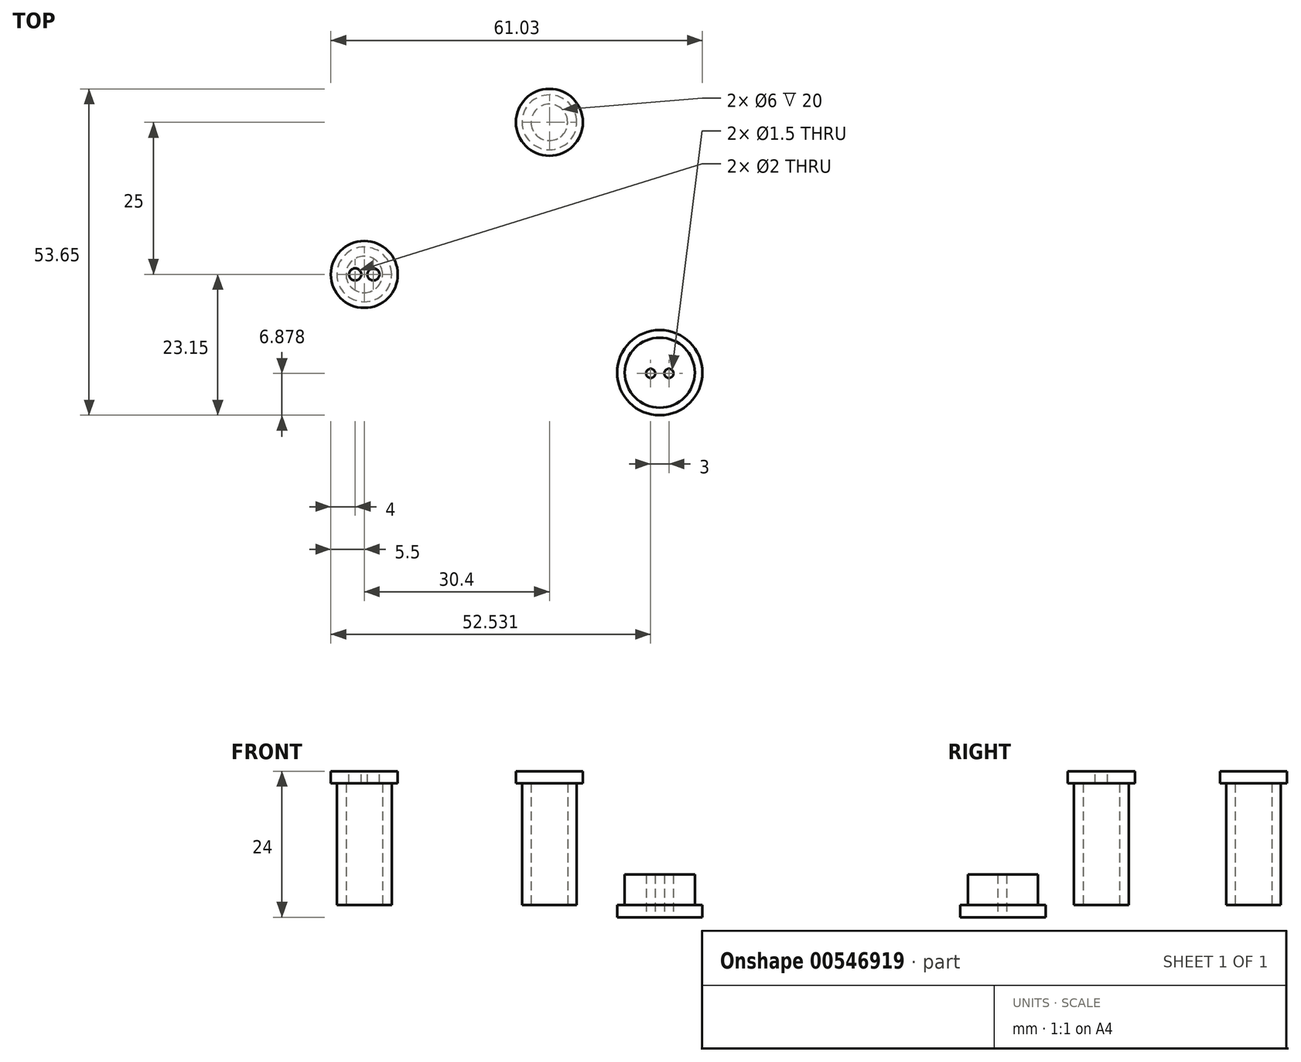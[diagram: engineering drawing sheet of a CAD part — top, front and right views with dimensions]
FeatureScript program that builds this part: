
annotation { "Feature Type Name" : "Feature", "Feature Type Description" : "" }
export const myFeature = defineFeature(function(context is Context, id is Id, definition is map)
    precondition{}
    {
        {
            var Q0;
            Q0=qCreatedBy(makeId("Top.planeOp"),FACE);
            var sketch = newSketch(context, id + "F0", { "sketchPlane" : qUnion([Q0])});
            skCircle(sketch, "E0", {"center": v(0, 0) * mm, "radius": 4.5 * mm});
            skSolve(sketch);
        }
        {
            var Q0;
            Q0=makeQuery(id+"F0.imprint","IMPRINT",FACE,{"disambiguationData":[TD([[makeQuery(id+"F0.imprint","IMPRINT",EDGE,{"derivedFrom":sQuery(id+"F0.wireOp",EDGE,"E0")}),1.0]])]});
            extrude(context, id + "F1", {"entities" : qUnion([Q0]), "depth" : 20 * mm, "offsetDistance" : 25 * mm});
        }
        {
            var Q0;
            Q0=makeQuery(id+"F1.opExtrude","CAP_FACE",FACE,{"disambiguationData":[OSD([sQuery(id+"F0.wireOp",EDGE,"E0")])],"isStart":false});
            var sketch = newSketch(context, id + "F2", { "sketchPlane" : qUnion([Q0])});
            skCircle(sketch, "E1", {"center": v(0, 0) * mm, "radius": 5.5 * mm});
            skSolve(sketch);
        }
        {
            var Q0;
            Q0=makeQuery(id+"F2.imprint","IMPRINT",FACE,{"disambiguationData":[TD([[makeQuery(id+"F2.imprint","IMPRINT",EDGE,{"derivedFrom":sQuery(id+"F2.wireOp",EDGE,"E1")}),1.0]])]});
            var Q1;
            Q1=makeQuery(id+"F2.imprint","IMPRINT",FACE,{"disambiguationData":[TD([[makeQuery(id+"F2.imprint","IMPRINT",EDGE,{"derivedFrom":makeQuery(id+"F1.opExtrude","CAP_EDGE",EDGE,{"disambiguationData":[OSD([sQuery(id+"F0.wireOp",EDGE,"E0")])],"isStart":false})}),1.0]])]});
            extrude(context, id + "F3", {"entities" : qUnion([Q0, Q1]), "operationType" : NewBodyOperationType.ADD, "depth" : 2 * mm, "offsetDistance" : 25 * mm});
        }
        {
            var Q0;
            Q0=makeQuery(id+"F1.opExtrude","CAP_FACE",FACE,{"disambiguationData":[OSD([sQuery(id+"F0.wireOp",EDGE,"E0")])],"isStart":true});
            var sketch = newSketch(context, id + "F4", { "sketchPlane" : qUnion([Q0])});
            skCircle(sketch, "E2", {"center": v(0, 0) * mm, "radius": 3 * mm});
            skSolve(sketch);
        }
        {
            var Q0;
            Q0=makeQuery(id+"F4.imprint","IMPRINT",FACE,{"disambiguationData":[TD([[makeQuery(id+"F4.imprint","IMPRINT",EDGE,{"derivedFrom":sQuery(id+"F4.wireOp",EDGE,"E2")}),1.0]])]});
            var Q1;
            Q1=makeQuery(id+"F3.opExtrude","CAP_FACE",FACE,{"disambiguationData":[OSD([sQuery(id+"F2.wireOp",EDGE,"E1")])],"isStart":true});
            extrude(context, id + "F5", {"entities" : qUnion([Q0]), "operationType" : NewBodyOperationType.REMOVE, "endBound" : BoundingType.UP_TO_SURFACE, "oppositeDirection" : true, "depth" : 25 * mm, "endBoundEntityFace" : qUnion([Q1]), "offsetDistance" : 25 * mm});
        }
        {
            var Q0;
            Q0=qCreatedBy(makeId("Top.planeOp"),FACE);
            var sketch = newSketch(context, id + "F6", { "sketchPlane" : qUnion([Q0])});
            skCircle(sketch, "E3", {"center": v(48.53, -16.15) * mm, "radius": 5.75 * mm});
            skSolve(sketch);
        }
        {
            var Q0;
            Q0=makeQuery(id+"F6.imprint","IMPRINT",FACE,{"disambiguationData":[TD([[makeQuery(id+"F6.imprint","IMPRINT",EDGE,{"derivedFrom":sQuery(id+"F6.wireOp",EDGE,"E3")}),1.0]])]});
            extrude(context, id + "F7", {"entities" : qUnion([Q0]), "depth" : 5 * mm, "offsetDistance" : 25 * mm});
        }
        {
            var Q0;
            Q0=makeQuery(id+"F7.opExtrude","CAP_FACE",FACE,{"disambiguationData":[OSD([sQuery(id+"F6.wireOp",EDGE,"E3")])],"isStart":true});
            var sketch = newSketch(context, id + "F8", { "sketchPlane" : qUnion([Q0])});
            skCircle(sketch, "E4", {"center": v(50.03, 16.27) * mm, "radius": 0.75 * mm});
            skCircle(sketch, "E5", {"center": v(47.03, 16.27) * mm, "radius": 0.75 * mm});
            skLineSegment(sketch, "E6", {"start": v(48.53, 16.15) * mm, "end": v(48.53, 18.57) * mm});
            skSolve(sketch);
        }
        {
            var Q0;
            Q0=makeQuery(id+"F8.imprint","IMPRINT",FACE,{"disambiguationData":[TD([[makeQuery(id+"F8.imprint","IMPRINT",EDGE,{"derivedFrom":sQuery(id+"F8.wireOp",EDGE,"E5")}),1.0]])]});
            var Q1;
            Q1=makeQuery(id+"F8.imprint","IMPRINT",FACE,{"disambiguationData":[TD([[makeQuery(id+"F8.imprint","IMPRINT",EDGE,{"derivedFrom":sQuery(id+"F8.wireOp",EDGE,"E4")}),1.0]])]});
            extrude(context, id + "F9", {"entities" : qUnion([Q0, Q1]), "operationType" : NewBodyOperationType.REMOVE, "endBound" : BoundingType.THROUGH_ALL, "oppositeDirection" : true, "depth" : 25 * mm, "offsetDistance" : 25 * mm});
        }
        {
            var Q0;
            Q0=makeQuery(id+"F7.opExtrude","CAP_FACE",FACE,{"disambiguationData":[OSD([sQuery(id+"F6.wireOp",EDGE,"E3")])],"isStart":true});
            var sketch = newSketch(context, id + "F10", { "sketchPlane" : qUnion([Q0])});
            skCircle(sketch, "E7", {"center": v(48.53, 16.15) * mm, "radius": 7 * mm});
            skSolve(sketch);
        }
        {
            var Q0;
            Q0=makeQuery(id+"F10.imprint","IMPRINT",FACE,{"disambiguationData":[TD([[makeQuery(id+"F10.imprint","IMPRINT",EDGE,{"derivedFrom":sQuery(id+"F10.wireOp",EDGE,"E7")}),1.0]])]});
            var Q1;
            Q1=makeQuery(id+"F10.imprint","IMPRINT",FACE,{"disambiguationData":[TD([[makeQuery(id+"F10.imprint","IMPRINT",EDGE,{"derivedFrom":makeQuery(id+"F7.opExtrude","CAP_EDGE",EDGE,{"disambiguationData":[OSD([sQuery(id+"F6.wireOp",EDGE,"E3")])],"isStart":true})}),-1.0]])]});
            extrude(context, id + "F11", {"entities" : qUnion([Q0, Q1]), "operationType" : NewBodyOperationType.ADD, "depth" : 2 * mm, "offsetDistance" : 25 * mm});
        }
        {
            var Q0;
            Q0=makeQuery(id+"F1.opExtrude","SWEPT_BODY",BODY,{"disambiguationData":[OSD([sQuery(id+"F0.wireOp",EDGE,"E0")])]});
            transform(context, id + "F12", {"entities" : qUnion([Q0]), "transformType" : TransformType.TRANSLATION_3D, "dx" : 30.4 * mm, "dy" : 25 * mm, "dz" : 0 * mm, "makeCopy" : true});
        }
        {
            var Q0;
            Q0=makeQuery(id+"F3.opExtrude","CAP_FACE",FACE,{"disambiguationData":[OSD([sQuery(id+"F2.wireOp",EDGE,"E1")])],"isStart":false});
            var sketch = newSketch(context, id + "F13", { "sketchPlane" : qUnion([Q0])});
            skLineSegment(sketch, "E8", {"start": v(0, 0) * mm, "end": v(0, 1.33) * mm});
            skLineSegment(sketch, "E9", {"start": v(0, 0) * mm, "end": v(0.98, 0) * mm});
            skCircle(sketch, "E10", {"center": v(-1.5, 0) * mm, "radius": 1 * mm});
            skCircle(sketch, "E11", {"center": v(1.5, 0) * mm, "radius": 1 * mm});
            skSolve(sketch);
        }
        {
            var Q0;
            Q0=makeQuery(id+"F13.imprint","IMPRINT",FACE,{"disambiguationData":[TD([[makeQuery(id+"F13.imprint","IMPRINT",EDGE,{"derivedFrom":sQuery(id+"F13.wireOp",EDGE,"E10")}),1.0]])]});
            var Q1;
            Q1=makeQuery(id+"F13.imprint","IMPRINT",FACE,{"disambiguationData":[TD([[makeQuery(id+"F13.imprint","IMPRINT",EDGE,{"derivedFrom":sQuery(id+"F13.wireOp",EDGE,"E11")}),1.0]])]});
            extrude(context, id + "F14", {"entities" : qUnion([Q0, Q1]), "operationType" : NewBodyOperationType.REMOVE, "endBound" : BoundingType.THROUGH_ALL, "oppositeDirection" : true, "depth" : 25 * mm, "offsetDistance" : 25 * mm});
        }
    });
